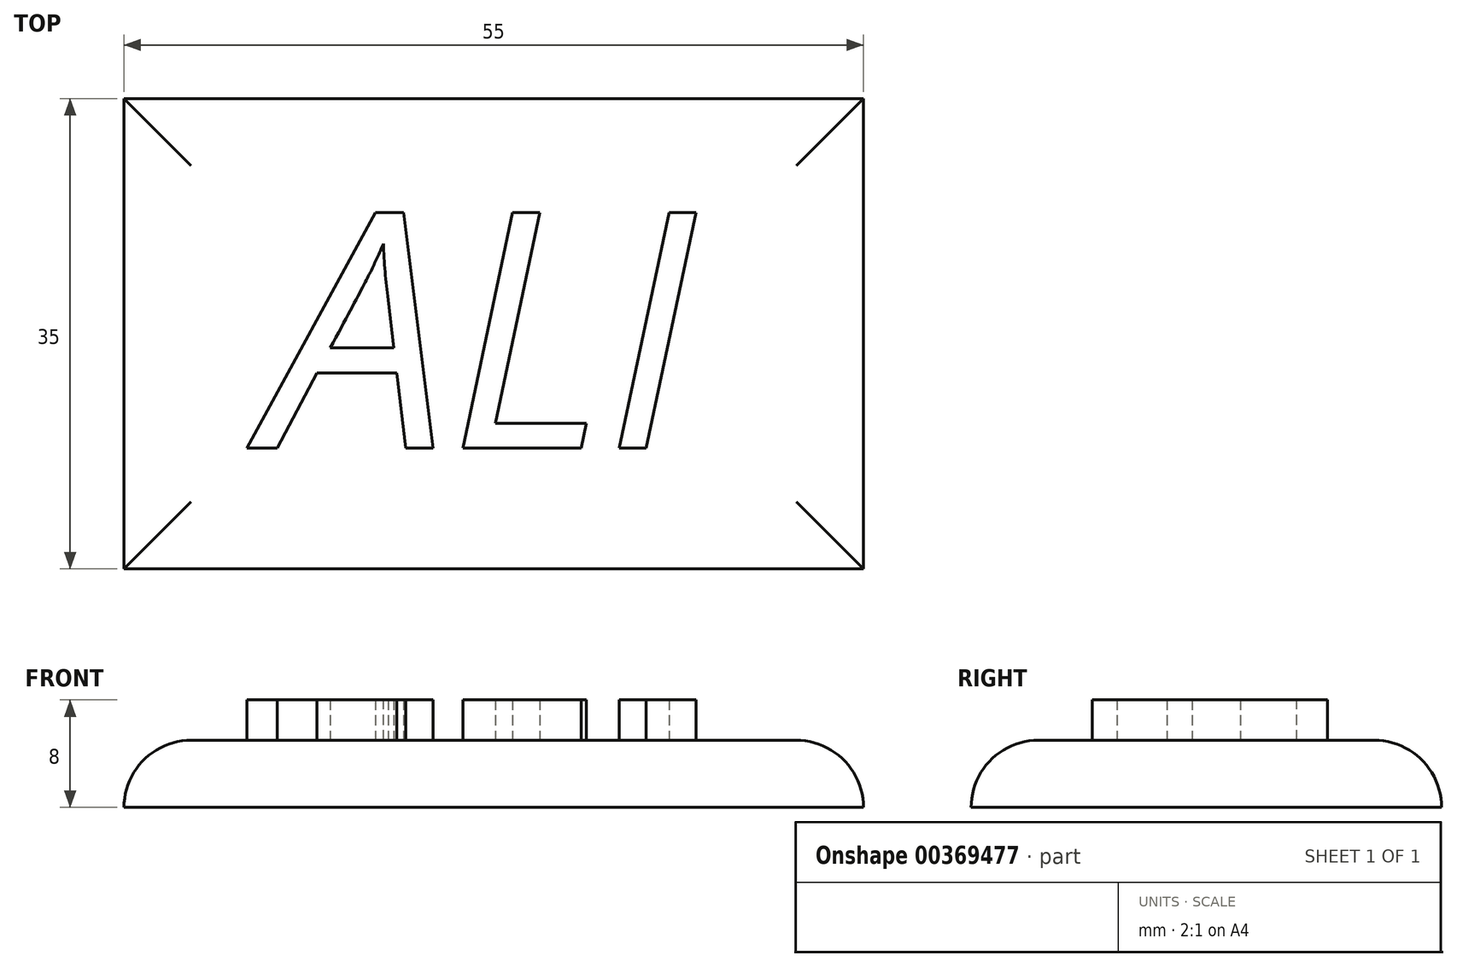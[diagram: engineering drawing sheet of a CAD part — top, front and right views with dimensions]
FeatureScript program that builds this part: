
annotation { "Feature Type Name" : "Feature", "Feature Type Description" : "" }
export const myFeature = defineFeature(function(context is Context, id is Id, definition is map)
    precondition{}
    {
        {
            var Q0;
            Q0=qCreatedBy(makeId("Top.planeOp"),FACE);
            var sketch = newSketch(context, id + "F0", { "sketchPlane" : qUnion([Q0])});
            skLineSegment(sketch, "E0.bottom", {"start": v(27.5, -17.5) * mm, "end": v(-27.5, -17.5) * mm});
            skLineSegment(sketch, "E0.top", {"start": v(27.5, 17.5) * mm, "end": v(-27.5, 17.5) * mm});
            skLineSegment(sketch, "E0.left", {"start": v(27.5, -17.5) * mm, "end": v(27.5, 17.5) * mm});
            skLineSegment(sketch, "E0.right", {"start": v(-27.5, -17.5) * mm, "end": v(-27.5, 17.5) * mm});
            skPoint(sketch, "E0.middle", {"position": v(0, 0) * mm});
            skSolve(sketch);
        }
        {
            var Q0;
            Q0 = qSketchRegion(id + "F0", true);
            extrude(context, id + "F1", {"entities" : qUnion([Q0]), "depth" : 5 * mm});
        }
        {
            var Q0;
            Q0=makeQuery(id+"F1.opExtrude","CAP_EDGE",EDGE,{"disambiguationData":[OSD([sQuery(id+"F0.wireOp",EDGE,"E0.right")])],"isStart":false});
            var Q1;
            Q1=makeQuery(id+"F1.opExtrude","CAP_EDGE",EDGE,{"disambiguationData":[OSD([sQuery(id+"F0.wireOp",EDGE,"E0.left")])],"isStart":false});
            var Q2;
            Q2=makeQuery(id+"F1.opExtrude","CAP_EDGE",EDGE,{"disambiguationData":[OSD([sQuery(id+"F0.wireOp",EDGE,"E0.bottom")])],"isStart":false});
            var Q3;
            Q3=makeQuery(id+"F1.opExtrude","CAP_EDGE",EDGE,{"disambiguationData":[OSD([sQuery(id+"F0.wireOp",EDGE,"E0.top")])],"isStart":false});
            fillet(context, id + "F2", {"entities" : qUnion([Q0, Q1, Q2, Q3]), "radius" : 5 * mm, "tangentPropagation" : true, "allowEdgeOverflow" : false});
        }
        {
            var Q0;
            Q0=makeQuery(id+"F1.opExtrude","CAP_FACE",FACE,{"disambiguationData":[OSD([sQuery(id+"F0.wireOp",EDGE,"E0.bottom"),sQuery(id+"F0.wireOp",EDGE,"E0.top"),sQuery(id+"F0.wireOp",EDGE,"E0.left"),sQuery(id+"F0.wireOp",EDGE,"E0.right")])],"isStart":false});
            var sketch = newSketch(context, id + "F3", { "sketchPlane" : qUnion([Q0])});
            skText(sketch, "E1", { "text": "ALI", "fontName": "OpenSans-Italic.ttf"});
            const initialGuessF3  = {"E1": [-0.01695, -0.0085, 1, 0, 0.01766]};
            skSetInitialGuess(sketch, initialGuessF3);
            skSolve(sketch);
        }
        {
            var Q0;
            Q0 = qSketchRegion(id + "F3", true);
            extrude(context, id + "F4", {"entities" : qUnion([Q0]), "operationType" : NewBodyOperationType.ADD, "depth" : 3 * mm});
        }
    });
